# Revit family: QMXLE
name_source: partatom
category: Mechanical Equipment
units: mm (PartAtom-declared; Revit-internal decimal feet)

## family parameters
Always vertical = Yes
Cut with Voids When Loaded = No
Part Type = Normal
Room Calculation Point = No
Round Connector Dimension = Use Diameter
Shared = No
Work Plane-Based = No

## types (32) — shared parameters
Five = 5"
Four = 4"
Manufacturer = Loren Cook Company
ONE EIGTH = 1/8"
One = 1"
One_and_a_half = 1 1/2"
Three = 3"
Two = 2"
Two_Feet = 24"
URL = www.lorencook.com
Zero = 0"

## per-type parameters (varying)
- 90_QMXLE: A_SUB=120"; A_half=60"; B_SUB=3"; B_SUB2=2 7/8"; B_SUB_Half=1 1/2"; CURB_OD=27 3/16"; CURB_OD_HALF=13 19/32"; C_SUB=30"; D_SUB=15"; D_SUB/2=7 1/2"; E_SUB=32 5/16"; E_SUB/2=16 5/32"; FAN_DIA=12 13/16"; FAN_RADIUS=6 13/32"; FAN_RADIUS_FIFTH=1 9/32"; FAN_RAD_Plus=7 29/32"; FRA=4 13/16"; F_SUB=21 3/8"; F_SUB/2=10 11/16"; F_SUB/4=5 11/32"; Inlet_Connection=21"; Model=QMXLE; TSQ2=13 7/8"; T_SQ=28"; T_SQ/2=14"; Type Comments=Mixed-Flow Upblast Laboratory Exhaust Blower Low Pressure Belt Drive Arrangement 9
- 300_QMXLE: A_SUB=123 11/16"; A_half=61 27/32"; B_SUB=3"; B_SUB2=2 7/8"; B_SUB_Half=1 1/2"; CURB_OD=50 15/16"; CURB_OD_HALF=25 15/32"; C_SUB=67"; D_SUB=39 1/8"; D_SUB/2=19 9/16"; E_SUB=63 1/4"; E_SUB/2=31 5/8"; FAN_DIA=42 1/2"; FAN_RADIUS=21 1/4"; FAN_RADIUS_FIFTH=4 1/4"; FAN_RAD_Plus=22 3/4"; FRA=15 15/16"; F_SUB=51 3/16"; F_SUB/2=25 19/32"; F_SUB/4=12 13/16"; Inlet_Connection=44 3/4"; Model=QMXLE; TSQ2=25 7/8"; T_SQ=52"; T_SQ/2=26"; Type Comments=Mixed-Flow Upblast Laboratory Exhaust Blower Low Pressure Belt Drive Arrangement 9
- 120_QMXLE: A_SUB=120"; A_half=60"; B_SUB=3"; B_SUB2=2 7/8"; B_SUB_Half=1 1/2"; CURB_OD=27 3/16"; CURB_OD_HALF=13 19/32"; C_SUB=37"; D_SUB=17"; D_SUB/2=8 1/2"; E_SUB=34 15/16"; E_SUB/2=17 15/32"; FAN_DIA=17 1/16"; FAN_RADIUS=8 17/32"; FAN_RADIUS_FIFTH=1 23/32"; FAN_RAD_Plus=10 1/32"; FRA=6 13/32"; F_SUB=25 5/8"; F_SUB/2=12 13/16"; F_SUB/4=6 13/32"; Inlet_Connection=21"; Model=QMXLE; TSQ2=13 7/8"; T_SQ=28"; T_SQ/2=14"; Type Comments=Mixed-Flow Upblast Laboratory Exhaust Blower Low Pressure Belt Drive Arrangement 9
- 135_QMXLE: A_SUB=120"; A_half=60"; B_SUB=3"; B_SUB2=2 7/8"; B_SUB_Half=1 1/2"; CURB_OD=27 1/8"; CURB_OD_HALF=13 9/16"; C_SUB=39"; D_SUB=18"; D_SUB/2=9"; E_SUB=36 7/16"; E_SUB/2=18 7/32"; FAN_DIA=19 1/4"; FAN_RADIUS=9 5/8"; FAN_RADIUS_FIFTH=1 15/16"; FAN_RAD_Plus=11 1/8"; FRA=7 7/32"; F_SUB=27 3/4"; F_SUB/2=13 7/8"; F_SUB/4=6 15/16"; Inlet_Connection=20 15/16"; Model=QMXLE; TSQ2=13 7/8"; T_SQ=28"; T_SQ/2=14"; Type Comments=Mixed-Flow Upblast Laboratory Exhaust Blower Low Pressure Belt Drive Arrangement 9
- 165_QMXLE: A_SUB=120"; A_half=60"; B_SUB=3"; B_SUB2=2 7/8"; B_SUB_Half=1 1/2"; CURB_OD=31 1/8"; CURB_OD_HALF=15 9/16"; C_SUB=44"; D_SUB=21"; D_SUB/2=10 1/2"; E_SUB=42 7/16"; E_SUB/2=21 7/32"; FAN_DIA=23 1/2"; FAN_RADIUS=11 3/4"; FAN_RADIUS_FIFTH=2 11/32"; FAN_RAD_Plus=13 1/4"; FRA=8 13/16"; F_SUB=31 11/16"; F_SUB/2=15 27/32"; F_SUB/4=7 15/16"; Inlet_Connection=24 15/16"; Model=QMXLE; TSQ2=15 7/8"; T_SQ=32"; T_SQ/2=16"; Type Comments=Mixed-Flow Upblast Laboratory Exhaust Blower Low Pressure Belt Drive Arrangement 9
- 180_QMXLE: A_SUB=120"; A_half=60"; B_SUB=3"; B_SUB2=2 7/8"; B_SUB_Half=1 1/2"; CURB_OD=33 1/8"; CURB_OD_HALF=16 9/16"; C_SUB=46"; D_SUB=23"; D_SUB/2=11 1/2"; E_SUB=44 1/4"; E_SUB/2=22 1/8"; FAN_DIA=25 5/8"; FAN_RADIUS=12 13/16"; FAN_RADIUS_FIFTH=2 9/16"; FAN_RAD_Plus=14 5/16"; FRA=9 5/8"; F_SUB=34 1/16"; F_SUB/2=17 1/32"; F_SUB/4=8 17/32"; Inlet_Connection=26 15/16"; Model=QMXLE; TSQ2=16 7/8"; T_SQ=34"; T_SQ/2=17"; Type Comments=Mixed-Flow Upblast Laboratory Exhaust Blower Low Pressure Belt Drive Arrangement 9
- 202_QMXLE: A_SUB=120"; A_half=60"; B_SUB=3"; B_SUB2=2 7/8"; B_SUB_Half=1 1/2"; CURB_OD=36 15/16"; CURB_OD_HALF=18 15/32"; C_SUB=50"; D_SUB=25 1/2"; D_SUB/2=12 3/4"; E_SUB=46 3/4"; E_SUB/2=23 3/8"; FAN_DIA=25 5/8"; FAN_RADIUS=12 13/16"; FAN_RADIUS_FIFTH=2 9/16"; FAN_RAD_Plus=14 5/16"; FRA=9 5/8"; F_SUB=37 15/16"; F_SUB/2=18 31/32"; F_SUB/4=9 1/2"; Inlet_Connection=30 3/4"; Model=QMXLE; TSQ2=18 7/8"; T_SQ=38"; T_SQ/2=19"; Type Comments=Mixed-Flow Upblast Laboratory Exhaust Blower Low Pressure Belt Drive Arrangement 9
- 225_QMXLE: A_SUB=120"; A_half=60"; B_SUB=3"; B_SUB2=2 7/8"; B_SUB_Half=1 1/2"; CURB_OD=40 15/16"; CURB_OD_HALF=20 15/32"; C_SUB=56"; D_SUB=27 1/2"; D_SUB/2=13 3/4"; E_SUB=50 1/4"; E_SUB/2=25 1/8"; FAN_DIA=31 15/16"; FAN_RADIUS=15 31/32"; FAN_RADIUS_FIFTH=3 3/16"; FAN_RAD_Plus=17 15/32"; FRA=11 31/32"; F_SUB=41 1/8"; F_SUB/2=20 9/16"; F_SUB/4=10 9/32"; Inlet_Connection=34 3/4"; Model=QMXLE; TSQ2=20 7/8"; T_SQ=42"; T_SQ/2=21"; Type Comments=Mixed-Flow Upblast Laboratory Exhaust Blower Low Pressure Belt Drive Arrangement 9
- 245_QMXLE: A_SUB=120"; A_half=60"; B_SUB=3"; B_SUB2=2 7/8"; B_SUB_Half=1 1/2"; CURB_OD=42 15/16"; CURB_OD_HALF=21 15/32"; C_SUB=59"; D_SUB=31 5/8"; D_SUB/2=15 13/16"; E_SUB=53 3/4"; E_SUB/2=26 7/8"; FAN_DIA=34 3/4"; FAN_RADIUS=17 3/8"; FAN_RADIUS_FIFTH=3 15/32"; FAN_RAD_Plus=18 7/8"; FRA=13 1/32"; F_SUB=43 7/16"; F_SUB/2=21 23/32"; F_SUB/4=10 7/8"; Inlet_Connection=36 3/4"; Model=QMXLE; TSQ2=21 7/8"; T_SQ=44"; T_SQ/2=22"; Type Comments=Mixed-Flow Upblast Laboratory Exhaust Blower Low Pressure Belt Drive Arrangement 9
- 270_QMXLE: A_SUB=120"; A_half=60"; B_SUB=3"; B_SUB2=2 7/8"; B_SUB_Half=1 1/2"; CURB_OD=46 15/16"; CURB_OD_HALF=23 15/32"; C_SUB=63"; D_SUB=35"; D_SUB/2=17 1/2"; E_SUB=56 1/4"; E_SUB/2=28 1/8"; FAN_DIA=38 5/16"; FAN_RADIUS=19 5/32"; FAN_RADIUS_FIFTH=3 27/32"; FAN_RAD_Plus=20 21/32"; FRA=14 3/8"; F_SUB=47"; F_SUB/2=23 1/2"; F_SUB/4=11 3/4"; Inlet_Connection=40 3/4"; Model=QMXLE; TSQ2=23 7/8"; T_SQ=48"; T_SQ/2=24"; Type Comments=Mixed-Flow Upblast Laboratory Exhaust Blower Low Pressure Belt Drive Arrangement 9
- 330_QMXLE: A_SUB=135 1/8"; A_half=67 9/16"; B_SUB=3"; B_SUB2=2 7/8"; B_SUB_Half=1 1/2"; CURB_OD=54 13/16"; CURB_OD_HALF=27 13/32"; C_SUB=73"; D_SUB=44"; D_SUB/2=22"; E_SUB=67 3/4"; E_SUB/2=33 7/8"; FAN_DIA=46 3/4"; FAN_RADIUS=23 3/8"; FAN_RADIUS_FIFTH=4 11/16"; FAN_RAD_Plus=24 7/8"; FRA=17 17/32"; F_SUB=55 15/16"; F_SUB/2=27 31/32"; F_SUB/4=14"; Inlet_Connection=48 5/8"; Model=QMXLE; TSQ2=27 7/8"; T_SQ=56"; T_SQ/2=28"; Type Comments=Mixed-Flow Upblast Laboratory Exhaust Blower Low Pressure Belt Drive Arrangement 9
- 365_QMXLE: A_SUB=146 1/2"; A_half=73 1/4"; B_SUB=3"; B_SUB2=2 7/8"; B_SUB_Half=1 1/2"; CURB_OD=63 3/4"; CURB_OD_HALF=31 7/8"; C_SUB=79"; D_SUB=47 1/2"; D_SUB/2=23 3/4"; E_SUB=73 1/4"; E_SUB/2=36 5/8"; FAN_DIA=51 3/4"; FAN_RADIUS=25 7/8"; FAN_RADIUS_FIFTH=5 3/16"; FAN_RAD_Plus=27 3/8"; FRA=19 13/32"; F_SUB=61 15/16"; F_SUB/2=30 31/32"; F_SUB/4=15 1/2"; Inlet_Connection=54 9/16"; Model=QMXLE; TSQ2=30 7/8"; T_SQ=62"; T_SQ/2=31"; Type Comments=Mixed-Flow Upblast Laboratory Exhaust Blower Low Pressure Belt Drive Arrangement 9
- 402_QMXLE: A_SUB=159 1/16"; A_half=79 17/32"; B_SUB=3"; B_SUB2=2 7/8"; B_SUB_Half=1 1/2"; CURB_OD=65 3/4"; CURB_OD_HALF=32 7/8"; C_SUB=88"; D_SUB=53 1/8"; D_SUB/2=26 9/16"; E_SUB=77 3/4"; E_SUB/2=38 7/8"; FAN_DIA=56 15/16"; FAN_RADIUS=28 15/32"; FAN_RADIUS_FIFTH=5 11/16"; FAN_RAD_Plus=29 31/32"; FRA=21 11/32"; F_SUB=67 1/8"; F_SUB/2=33 9/16"; F_SUB/4=16 25/32"; Inlet_Connection=59 7/16"; Model=QMXLE; TSQ2=33 3/8"; T_SQ=67"; T_SQ/2=33 1/2"; Type Comments=Mixed-Flow Upblast Laboratory Exhaust Blower Low Pressure Belt Drive Arrangement 9
- 445_QMXLE: A_SUB=173 7/16"; A_half=86 23/32"; B_SUB=3"; B_SUB2=2 7/8"; B_SUB_Half=1 1/2"; CURB_OD=72 5/8"; CURB_OD_HALF=36 5/16"; C_SUB=95"; D_SUB=59 1/8"; D_SUB/2=29 9/16"; E_SUB=83 1/4"; E_SUB/2=41 5/8"; FAN_DIA=63 1/16"; FAN_RADIUS=31 17/32"; FAN_RADIUS_FIFTH=6 5/16"; FAN_RAD_Plus=33 1/32"; FRA=23 21/32"; F_SUB=73 1/4"; F_SUB/2=36 5/8"; F_SUB/4=18 5/16"; Inlet_Connection=66 7/16"; Model=QMXLE; TSQ2=36 7/8"; T_SQ=74"; T_SQ/2=37"; Type Comments=Mixed-Flow Upblast Laboratory Exhaust Blower Low Pressure Belt Drive Arrangement 9
- 490_QMXLE: A_SUB=186"; A_half=93"; B_SUB=4"; B_SUB2=3 7/8"; B_SUB_Half=2"; CURB_OD=78 1/2"; CURB_OD_HALF=39 1/4"; C_SUB=103"; D_SUB=61 1/8"; D_SUB/2=30 9/16"; E_SUB=90 3/4"; E_SUB/2=45 3/8"; FAN_DIA=69 3/8"; FAN_RADIUS=34 11/16"; FAN_RADIUS_FIFTH=6 15/16"; FAN_RAD_Plus=36 3/16"; FRA=26 1/32"; F_SUB=79 9/16"; F_SUB/2=39 25/32"; F_SUB/4=19 29/32"; Inlet_Connection=72 1/4"; Model=QMXLE; TSQ2=39 7/8"; T_SQ=80"; T_SQ/2=40"; Type Comments=Mixed-Flow Upblast Laboratory Exhaust Blower Low Pressure Belt Drive Arrangement 9
- 150_QMXLE: A_SUB=120"; A_half=60"; B_SUB=3"; B_SUB2=2 7/8"; B_SUB_Half=1 1/2"; CURB_OD=29 1/8"; CURB_OD_HALF=14 9/16"; C_SUB=42"; D_SUB=20"; D_SUB/2=10"; E_SUB=39 7/16"; E_SUB/2=19 23/32"; FAN_DIA=21 3/8"; FAN_RADIUS=10 11/16"; FAN_RADIUS_FIFTH=2 1/8"; FAN_RAD_Plus=12 3/16"; FRA=8 1/32"; F_SUB=29 9/16"; F_SUB/2=14 25/32"; F_SUB/4=7 13/32"; Inlet_Connection=22 15/16"; Model=QMXLE; TSQ2=14 7/8"; T_SQ=30"; T_SQ/2=15"; Type Comments=Mixed-Flow Upblast Laboratory Exhaust Blower Low Pressure Belt Drive Arrangement 9
- 120_QMXLE-HP: A_SUB=120"; A_half=60"; B_SUB=3"; B_SUB2=2 7/8"; B_SUB_Half=1 1/2"; CURB_OD=27 3/16"; CURB_OD_HALF=13 19/32"; C_SUB=37"; D_SUB=17"; D_SUB/2=8 1/2"; E_SUB=34 15/16"; E_SUB/2=17 15/32"; FAN_DIA=17 1/16"; FAN_RADIUS=8 17/32"; FAN_RADIUS_FIFTH=1 23/32"; FAN_RAD_Plus=10 1/32"; FRA=6 13/32"; F_SUB=25 5/8"; F_SUB/2=12 13/16"; F_SUB/4=6 13/32"; Inlet_Connection=21"; Model=QMXLE-HP; TSQ2=13 7/8"; T_SQ=28"; T_SQ/2=14"; Type Comments=Mixed-Flow Upblast Laboratory Exhaust Blower High Pressure Belt Drive Arrangement 9
- 135_QMXHPLE: A_SUB=120"; A_half=60"; B_SUB=3"; B_SUB2=2 7/8"; B_SUB_Half=1 1/2"; CURB_OD=27 1/8"; CURB_OD_HALF=13 9/16"; C_SUB=39"; D_SUB=18"; D_SUB/2=9"; E_SUB=36 7/16"; E_SUB/2=18 7/32"; FAN_DIA=19 1/4"; FAN_RADIUS=9 5/8"; FAN_RADIUS_FIFTH=1 15/16"; FAN_RAD_Plus=11 1/8"; FRA=7 7/32"; F_SUB=27 3/4"; F_SUB/2=13 7/8"; F_SUB/4=6 15/16"; Inlet_Connection=20 15/16"; Model=QMXLE-HP; TSQ2=13 7/8"; T_SQ=28"; T_SQ/2=14"; Type Comments=Mixed-Flow Upblast Laboratory Exhaust Blower High Pressure Belt Drive Arrangement 9
- 150_QMXHPLE: A_SUB=120"; A_half=60"; B_SUB=3"; B_SUB2=2 7/8"; B_SUB_Half=1 1/2"; CURB_OD=29 1/8"; CURB_OD_HALF=14 9/16"; C_SUB=42"; D_SUB=20"; D_SUB/2=10"; E_SUB=39 7/16"; E_SUB/2=19 23/32"; FAN_DIA=21 3/8"; FAN_RADIUS=10 11/16"; FAN_RADIUS_FIFTH=2 1/8"; FAN_RAD_Plus=12 3/16"; FRA=8 1/32"; F_SUB=29 9/16"; F_SUB/2=14 25/32"; F_SUB/4=7 13/32"; Inlet_Connection=22 15/16"; Model=QMXLE-HP; TSQ2=14 7/8"; T_SQ=30"; T_SQ/2=15"; Type Comments=Mixed-Flow Upblast Laboratory Exhaust Blower High Pressure Belt Drive Arrangement 9
- 165_QMXHPLE: A_SUB=120"; A_half=60"; B_SUB=3"; B_SUB2=2 7/8"; B_SUB_Half=1 1/2"; CURB_OD=31 1/8"; CURB_OD_HALF=15 9/16"; C_SUB=44"; D_SUB=21"; D_SUB/2=10 1/2"; E_SUB=42 7/16"; E_SUB/2=21 7/32"; FAN_DIA=23 1/2"; FAN_RADIUS=11 3/4"; FAN_RADIUS_FIFTH=2 11/32"; FAN_RAD_Plus=13 1/4"; FRA=8 13/16"; F_SUB=31 11/16"; F_SUB/2=15 27/32"; F_SUB/4=7 15/16"; Inlet_Connection=24 15/16"; Model=QMXLE-HP; TSQ2=15 7/8"; T_SQ=32"; T_SQ/2=16"; Type Comments=Mixed-Flow Upblast Laboratory Exhaust Blower High Pressure Belt Drive Arrangement 9
- 180_QMXHPLE: A_SUB=120"; A_half=60"; B_SUB=3"; B_SUB2=2 7/8"; B_SUB_Half=1 1/2"; CURB_OD=33 1/8"; CURB_OD_HALF=16 9/16"; C_SUB=46"; D_SUB=23"; D_SUB/2=11 1/2"; E_SUB=44 1/4"; E_SUB/2=22 1/8"; FAN_DIA=25 5/8"; FAN_RADIUS=12 13/16"; FAN_RADIUS_FIFTH=2 9/16"; FAN_RAD_Plus=14 5/16"; FRA=9 5/8"; F_SUB=34 1/16"; F_SUB/2=17 1/32"; F_SUB/4=8 17/32"; Inlet_Connection=26 15/16"; Model=QMXLE-HP; TSQ2=16 7/8"; T_SQ=34"; T_SQ/2=17"; Type Comments=Mixed-Flow Upblast Laboratory Exhaust Blower High Pressure Belt Drive Arrangement 9
- 202_QMXHPLE: A_SUB=120"; A_half=60"; B_SUB=3"; B_SUB2=2 7/8"; B_SUB_Half=1 1/2"; CURB_OD=36 15/16"; CURB_OD_HALF=18 15/32"; C_SUB=50"; D_SUB=25 1/2"; D_SUB/2=12 3/4"; E_SUB=46 3/4"; E_SUB/2=23 3/8"; FAN_DIA=25 5/8"; FAN_RADIUS=12 13/16"; FAN_RADIUS_FIFTH=2 9/16"; FAN_RAD_Plus=14 5/16"; FRA=9 5/8"; F_SUB=37 15/16"; F_SUB/2=18 31/32"; F_SUB/4=9 1/2"; Inlet_Connection=30 3/4"; Model=QMXLE-HP; TSQ2=18 7/8"; T_SQ=38"; T_SQ/2=19"; Type Comments=Mixed-Flow Upblast Laboratory Exhaust Blower High Pressure Belt Drive Arrangement 9
- 225_QMXHPLE: A_SUB=120"; A_half=60"; B_SUB=3"; B_SUB2=2 7/8"; B_SUB_Half=1 1/2"; CURB_OD=40 15/16"; CURB_OD_HALF=20 15/32"; C_SUB=56"; D_SUB=27 1/2"; D_SUB/2=13 3/4"; E_SUB=50 1/4"; E_SUB/2=25 1/8"; FAN_DIA=31 15/16"; FAN_RADIUS=15 31/32"; FAN_RADIUS_FIFTH=3 3/16"; FAN_RAD_Plus=17 15/32"; FRA=11 31/32"; F_SUB=41 1/8"; F_SUB/2=20 9/16"; F_SUB/4=10 9/32"; Inlet_Connection=34 3/4"; Model=QMXLE-HP; TSQ2=20 7/8"; T_SQ=42"; T_SQ/2=21"; Type Comments=Mixed-Flow Upblast Laboratory Exhaust Blower High Pressure Belt Drive Arrangement 9
- 245_QMXHPLE: A_SUB=120"; A_half=60"; B_SUB=3"; B_SUB2=2 7/8"; B_SUB_Half=1 1/2"; CURB_OD=42 15/16"; CURB_OD_HALF=21 15/32"; C_SUB=59"; D_SUB=31 5/8"; D_SUB/2=15 13/16"; E_SUB=53 3/4"; E_SUB/2=26 7/8"; FAN_DIA=34 3/4"; FAN_RADIUS=17 3/8"; FAN_RADIUS_FIFTH=3 15/32"; FAN_RAD_Plus=18 7/8"; FRA=13 1/32"; F_SUB=43 7/16"; F_SUB/2=21 23/32"; F_SUB/4=10 7/8"; Inlet_Connection=36 3/4"; Model=QMXLE-HP; TSQ2=21 7/8"; T_SQ=44"; T_SQ/2=22"; Type Comments=Mixed-Flow Upblast Laboratory Exhaust Blower High Pressure Belt Drive Arrangement 9
- 270_QMXHPLE: A_SUB=120"; A_half=60"; B_SUB=3"; B_SUB2=2 7/8"; B_SUB_Half=1 1/2"; CURB_OD=46 15/16"; CURB_OD_HALF=23 15/32"; C_SUB=63"; D_SUB=35"; D_SUB/2=17 1/2"; E_SUB=56 1/4"; E_SUB/2=28 1/8"; FAN_DIA=38 5/16"; FAN_RADIUS=19 5/32"; FAN_RADIUS_FIFTH=3 27/32"; FAN_RAD_Plus=20 21/32"; FRA=14 3/8"; F_SUB=47"; F_SUB/2=23 1/2"; F_SUB/4=11 3/4"; Inlet_Connection=40 3/4"; Model=QMXLE-HP; TSQ2=23 7/8"; T_SQ=48"; T_SQ/2=24"; Type Comments=Mixed-Flow Upblast Laboratory Exhaust Blower High Pressure Belt Drive Arrangement 9
- 300_QMXHPLE: A_SUB=123 11/16"; A_half=61 27/32"; B_SUB=3"; B_SUB2=2 7/8"; B_SUB_Half=1 1/2"; CURB_OD=50 15/16"; CURB_OD_HALF=25 15/32"; C_SUB=67"; D_SUB=39 1/8"; D_SUB/2=19 9/16"; E_SUB=63 1/4"; E_SUB/2=31 5/8"; FAN_DIA=42 1/2"; FAN_RADIUS=21 1/4"; FAN_RADIUS_FIFTH=4 1/4"; FAN_RAD_Plus=22 3/4"; FRA=15 15/16"; F_SUB=51 3/16"; F_SUB/2=25 19/32"; F_SUB/4=12 13/16"; Inlet_Connection=44 3/4"; Model=QMXLE-HP; TSQ2=25 7/8"; T_SQ=52"; T_SQ/2=26"; Type Comments=Mixed-Flow Upblast Laboratory Exhaust Blower High Pressure Belt Drive Arrangement 9
- 330_QMXHPLE: A_SUB=135 1/8"; A_half=67 9/16"; B_SUB=3"; B_SUB2=2 7/8"; B_SUB_Half=1 1/2"; CURB_OD=54 13/16"; CURB_OD_HALF=27 13/32"; C_SUB=73"; D_SUB=44"; D_SUB/2=22"; E_SUB=67 3/4"; E_SUB/2=33 7/8"; FAN_DIA=46 3/4"; FAN_RADIUS=23 3/8"; FAN_RADIUS_FIFTH=4 11/16"; FAN_RAD_Plus=24 7/8"; FRA=17 17/32"; F_SUB=55 15/16"; F_SUB/2=27 31/32"; F_SUB/4=14"; Inlet_Connection=48 5/8"; Model=QMXLE-HP; TSQ2=27 7/8"; T_SQ=56"; T_SQ/2=28"; Type Comments=Mixed-Flow Upblast Laboratory Exhaust Blower High Pressure Belt Drive Arrangement 9
- 365_QMXHPLE: A_SUB=146 1/2"; A_half=73 1/4"; B_SUB=3"; B_SUB2=2 7/8"; B_SUB_Half=1 1/2"; CURB_OD=63 3/4"; CURB_OD_HALF=31 7/8"; C_SUB=79"; D_SUB=47 1/2"; D_SUB/2=23 3/4"; E_SUB=73 1/4"; E_SUB/2=36 5/8"; FAN_DIA=51 3/4"; FAN_RADIUS=25 7/8"; FAN_RADIUS_FIFTH=5 3/16"; FAN_RAD_Plus=27 3/8"; FRA=19 13/32"; F_SUB=61 15/16"; F_SUB/2=30 31/32"; F_SUB/4=15 1/2"; Inlet_Connection=54 9/16"; Model=QMXLE-HP; TSQ2=30 7/8"; T_SQ=62"; T_SQ/2=31"; Type Comments=Mixed-Flow Upblast Laboratory Exhaust Blower High Pressure Belt Drive Arrangement 9
- 402_QMXHPLE: A_SUB=159 1/16"; A_half=79 17/32"; B_SUB=3"; B_SUB2=2 7/8"; B_SUB_Half=1 1/2"; CURB_OD=65 3/4"; CURB_OD_HALF=32 7/8"; C_SUB=88"; D_SUB=53 1/8"; D_SUB/2=26 9/16"; E_SUB=77 3/4"; E_SUB/2=38 7/8"; FAN_DIA=56 15/16"; FAN_RADIUS=28 15/32"; FAN_RADIUS_FIFTH=5 11/16"; FAN_RAD_Plus=29 31/32"; FRA=21 11/32"; F_SUB=67 1/8"; F_SUB/2=33 9/16"; F_SUB/4=16 25/32"; Inlet_Connection=59 7/16"; Model=QMXLE-HP; TSQ2=33 3/8"; T_SQ=67"; T_SQ/2=33 1/2"; Type Comments=Mixed-Flow Upblast Laboratory Exhaust Blower High Pressure Belt Drive Arrangement 9
- 445_QMXHPLE: A_SUB=173 7/16"; A_half=86 23/32"; B_SUB=3"; B_SUB2=2 7/8"; B_SUB_Half=1 1/2"; CURB_OD=72 5/8"; CURB_OD_HALF=36 5/16"; C_SUB=95"; D_SUB=59 1/8"; D_SUB/2=29 9/16"; E_SUB=83 1/4"; E_SUB/2=41 5/8"; FAN_DIA=63 1/16"; FAN_RADIUS=31 17/32"; FAN_RADIUS_FIFTH=6 5/16"; FAN_RAD_Plus=33 1/32"; FRA=23 21/32"; F_SUB=73 1/4"; F_SUB/2=36 5/8"; F_SUB/4=18 5/16"; Inlet_Connection=66 7/16"; Model=QMXLE-HP; TSQ2=36 7/8"; T_SQ=74"; T_SQ/2=37"; Type Comments=Mixed-Flow Upblast Laboratory Exhaust Blower High Pressure Belt Drive Arrangement 9
- 490_QMXHPLE: A_SUB=186"; A_half=93"; B_SUB=4"; B_SUB2=3 7/8"; B_SUB_Half=2"; CURB_OD=78 1/2"; CURB_OD_HALF=39 1/4"; C_SUB=103"; D_SUB=61 1/8"; D_SUB/2=30 9/16"; E_SUB=90 3/4"; E_SUB/2=45 3/8"; FAN_DIA=69 3/8"; FAN_RADIUS=34 11/16"; FAN_RADIUS_FIFTH=6 15/16"; FAN_RAD_Plus=36 3/16"; FRA=26 1/32"; F_SUB=79 9/16"; F_SUB/2=39 25/32"; F_SUB/4=19 29/32"; Inlet_Connection=72 1/4"; Model=QMXLE-HP; TSQ2=39 7/8"; T_SQ=80"; T_SQ/2=40"; Type Comments=Mixed-Flow Upblast Laboratory Exhaust Blower High Pressure Belt Drive Arrangement 9
- 90_QMXHPLE: A_SUB=120"; A_half=60"; B_SUB=3"; B_SUB2=2 7/8"; B_SUB_Half=1 1/2"; CURB_OD=27 3/16"; CURB_OD_HALF=13 19/32"; C_SUB=30"; D_SUB=15"; D_SUB/2=7 1/2"; E_SUB=32 5/16"; E_SUB/2=16 5/32"; FAN_DIA=12 13/16"; FAN_RADIUS=6 13/32"; FAN_RADIUS_FIFTH=1 9/32"; FAN_RAD_Plus=7 29/32"; FRA=4 13/16"; F_SUB=21 3/8"; F_SUB/2=10 11/16"; F_SUB/4=5 11/32"; Inlet_Connection=21"; Model=QMXLE-HP; TSQ2=13 7/8"; T_SQ=28"; T_SQ/2=14"; Type Comments=Mixed-Flow Upblast Laboratory Exhaust Blower High Pressure Belt Drive Arrangement 9

## geometry (parser evidence)
native form markers: Sweep x1
no freeform markers — native parametric forms only
